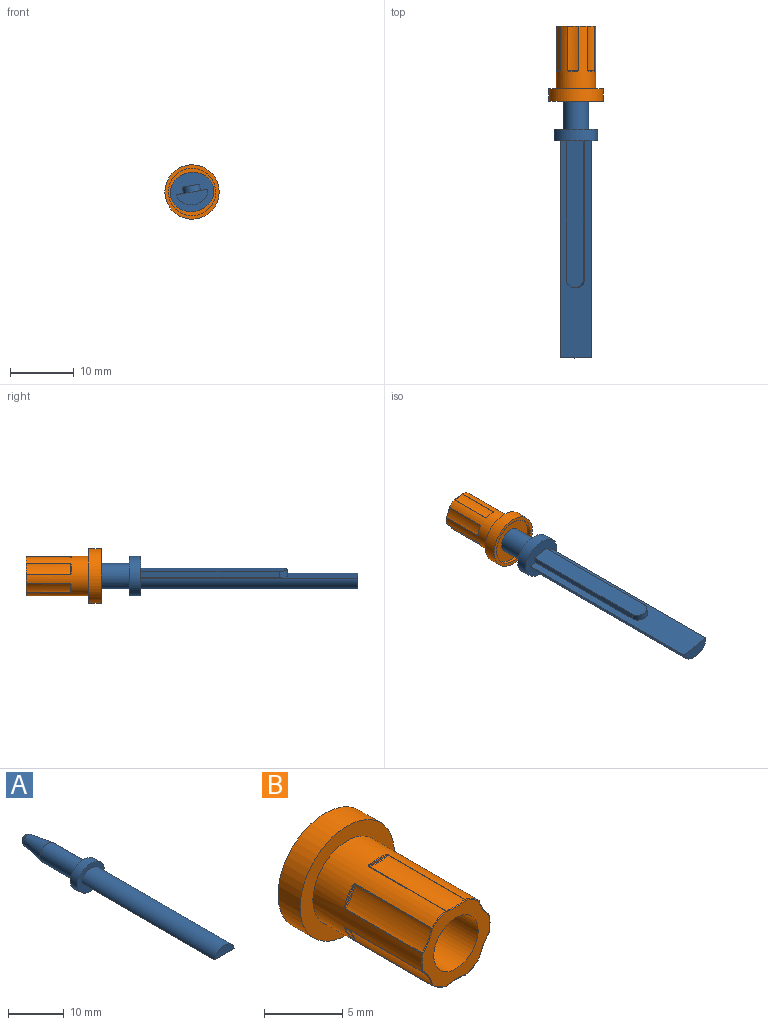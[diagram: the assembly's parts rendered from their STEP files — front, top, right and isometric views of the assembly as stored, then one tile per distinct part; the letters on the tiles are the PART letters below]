
ASSEMBLY  parts=2 mates=1
PART A: 14 faces, bbox 6.9x51x6.1 mm
  f0: plane 6.9x6.1mm, normal (0,-1,0), area 22.7mm2, adj f1,f2,f4,f10,f11,f13
  f1: plane 34x4.9mm, normal (0,0,-1), area 105.3mm2, adj f0,f2,f3,f10,f11,f12
  f2: extruded ~34x4.9mm, area 238.3mm2, adj f0,f1,f3
  f3: plane 4.9x2mm, normal (0,-1,0), area 7.7mm2, adj f1,f2
  f4: extruded ~6.9x6.1mm, area 36.8mm2, adj f0,f5
  f5: plane 6.9x6.1mm, normal (0,1,0), area 20.6mm2, adj f4,f6
  f6: cylinder r=1.99mm len=9.15mm, axis (0,-1,0), area 114.4mm2, adj f5,f8
  f7: plane 0.3x0.3mm, normal (0,1,0), area 0.1mm2, adj f9
  f8: bspline ~5.27x3.98mm, area 52.2mm2, adj f6,f9
  f9: bspline ~2.27x2.27mm, area 6.6mm2, adj f7,f8
  f10: plane 21.65x1mm, normal (-1,0,0), area 21.7mm2, adj f0,f1,f12,f13
  f11: plane 21.65x1mm, normal (1,0,0), area 21.7mm2, adj f0,f1,f12,f13
  f12: cylinder r=1.35mm len=2.7mm, axis (0,0,1), area 4.2mm2, adj f1,f10,f11,f13
  f13: plane 23x2.7mm, normal (0,0,-1), area 61.3mm2, adj f0,f10,f11,f12
PART B: 80 faces, bbox 8.5x11.8x8.5 mm
  f0: cylinder r=2mm len=11.2mm, axis (0,-1,0), area 140.7mm2, adj f5,f79
  f1: cylinder r=4.25mm len=8.5mm, axis (0,1,0), area 53.4mm2, adj f2,f3
  f2: plane 8.5x8.5mm, normal (0,-1,0), area 26.6mm2, adj f1,f4
  f3: plane 8.5x8.5mm, normal (0,1,0), area 13.5mm2, adj f1,f78
  f4: cylinder r=3.1mm len=9.75mm, axis (0,1,0), area 114.6mm2, adj f2,f8,f9,f11,f12,f13,f16,f17
  f5: plane 6.1x5.86mm, normal (0,-1,0), area 14.9mm2, adj f0,f54,f57,f58,f61,f62,f65,f66
  f6: extruded ~6.9x1.7mm, area 11.9mm2, adj f8,f10,f13,f66
  f7: plane 1.38x0.15mm, normal (0,-1,0), area 0.1mm2, adj f10,f11
  f8: cylinder r=0.05mm len=6.9mm, axis (0,-1,0), area 0.2mm2, adj f4,f6,f9,f64
  f9: bspline ~0.21x0.12mm, area 0mm2, adj f4,f8,f10,f11
  f10: bspline ~1.83x0.2mm, area 0.1mm2, adj f6,f7,f9,f12
  f11: torus R=3.05mm, axis (0,-1,0), area 0.1mm2, adj f4,f7,f9,f12
  f12: bspline ~0.31x0.11mm, area 0mm2, adj f4,f10,f11,f13
  f13: cylinder r=0.05mm len=6.9mm, axis (0,-1,0), area 0.2mm2, adj f4,f6,f12,f68
  f14: extruded ~6.9x1.48mm, area 11.9mm2, adj f16,f18,f21,f58
  f15: plane 1.2x0.68mm, normal (0,-1,0), area 0.1mm2, adj f18,f19
  f16: cylinder r=0.05mm len=6.9mm, axis (0,-1,0), area 0.2mm2, adj f4,f14,f17,f56
  f17: bspline ~0.2x0.12mm, area 0mm2, adj f4,f16,f18,f19
  f18: bspline ~1.49x0.87mm, area 0.1mm2, adj f14,f15,f17,f20
  f19: torus R=3.05mm, axis (0,-1,0), area 0.1mm2, adj f4,f15,f17,f20
  f20: bspline ~0.27x0.21mm, area 0mm2, adj f4,f18,f19,f21
  f21: cylinder r=0.05mm len=6.9mm, axis (0,-1,0), area 0.2mm2, adj f4,f14,f20,f60
  f22: extruded ~6.9x1.47mm, area 11.9mm2, adj f24,f26,f29,f57
  f23: plane 1.19x0.7mm, normal (0,-1,0), area 0.1mm2, adj f26,f27
  f24: cylinder r=0.05mm len=6.9mm, axis (0,-1,0), area 0.2mm2, adj f4,f22,f25,f59
  f25: bspline ~0.18x0.15mm, area 0mm2, adj f4,f24,f26,f27
  f26: bspline ~1.57x0.95mm, area 0.1mm2, adj f22,f23,f25,f28
  f27: torus R=3.05mm, axis (0,-1,0), area 0.1mm2, adj f4,f23,f25,f28
  f28: bspline ~0.3x0.16mm, area 0mm2, adj f4,f26,f27,f29
  f29: cylinder r=0.05mm len=6.9mm, axis (0,-1,0), area 0.2mm2, adj f4,f22,f28,f55
  f30: extruded ~6.9x1.7mm, area 11.9mm2, adj f32,f34,f37,f65
  f31: plane 1.38x0.15mm, normal (0,-1,0), area 0.1mm2, adj f34,f35
  f32: cylinder r=0.05mm len=6.9mm, axis (0,-1,0), area 0.2mm2, adj f4,f30,f33,f67
  f33: bspline ~0.21x0.12mm, area 0mm2, adj f4,f32,f34,f35
  f34: bspline ~1.83x0.2mm, area 0.1mm2, adj f30,f31,f33,f36
  f35: torus R=3.05mm, axis (0,-1,0), area 0.1mm2, adj f4,f31,f33,f36
  f36: bspline ~0.31x0.11mm, area 0mm2, adj f4,f34,f35,f37
  f37: cylinder r=0.05mm len=6.9mm, axis (0,-1,0), area 0.2mm2, adj f4,f30,f36,f63
  f38: extruded ~6.9x1.48mm, area 11.9mm2, adj f40,f42,f45,f73
  f39: plane 1.2x0.68mm, normal (0,-1,0), area 0.1mm2, adj f42,f43
  f40: cylinder r=0.05mm len=6.9mm, axis (0,-1,0), area 0.2mm2, adj f4,f38,f41,f75
  f41: bspline ~0.2x0.12mm, area 0mm2, adj f4,f40,f42,f43
  f42: bspline ~1.49x0.87mm, area 0.1mm2, adj f38,f39,f41,f44
  f43: torus R=3.05mm, axis (0,-1,0), area 0.1mm2, adj f4,f39,f41,f44
  f44: bspline ~0.27x0.21mm, area 0mm2, adj f4,f42,f43,f45
  f45: cylinder r=0.05mm len=6.9mm, axis (0,-1,0), area 0.2mm2, adj f4,f38,f44,f71
  f46: extruded ~6.9x1.47mm, area 11.9mm2, adj f48,f50,f53,f74
  f47: plane 1.19x0.7mm, normal (0,-1,0), area 0.1mm2, adj f50,f51
  f48: cylinder r=0.05mm len=6.9mm, axis (0,-1,0), area 0.2mm2, adj f4,f46,f49,f72
  f49: bspline ~0.18x0.15mm, area 0mm2, adj f4,f48,f50,f51
  f50: bspline ~1.57x0.95mm, area 0.1mm2, adj f46,f47,f49,f52
  f51: torus R=3.05mm, axis (0,-1,0), area 0.1mm2, adj f4,f47,f49,f52
  f52: bspline ~0.3x0.16mm, area 0mm2, adj f4,f50,f51,f53
  f53: cylinder r=0.05mm len=6.9mm, axis (0,-1,0), area 0.2mm2, adj f4,f46,f52,f76
  f54: torus R=3.05mm, axis (0,-1,0), area 0.1mm2, adj f4,f5,f55,f56
  f55: sphere r=0.05mm, area 0mm2, adj f29,f54,f57
  f56: sphere r=0.05mm, area 0mm2, adj f16,f54,f58
  f57: bspline ~1.62x0.97mm, area 0.1mm2, adj f5,f22,f55,f59
  f58: bspline ~1.63x0.96mm, area 0.1mm2, adj f5,f14,f56,f60
  f59: sphere r=0.05mm, area 0mm2, adj f24,f57,f61
  f60: sphere r=0.05mm, area 0mm2, adj f21,f58,f62
  f61: torus R=3.05mm, axis (0,-1,0), area 0.1mm2, adj f4,f5,f59,f63
  f62: torus R=3.05mm, axis (0,-1,0), area 0.1mm2, adj f4,f5,f60,f64
  f63: sphere r=0.05mm, area 0mm2, adj f37,f61,f65
  f64: sphere r=0.05mm, area 0mm2, adj f8,f62,f66
  f65: bspline ~1.87x0.2mm, area 0.1mm2, adj f5,f30,f63,f67
  f66: bspline ~1.87x0.2mm, area 0.1mm2, adj f5,f6,f64,f68
  f67: sphere r=0.05mm, area 0mm2, adj f32,f65,f69
  f68: sphere r=0.05mm, area 0mm2, adj f13,f66,f70
  f69: torus R=3.05mm, axis (0,-1,0), area 0.1mm2, adj f4,f5,f67,f71
  f70: torus R=3.05mm, axis (0,-1,0), area 0.1mm2, adj f4,f5,f68,f72
  f71: sphere r=0.05mm, area 0mm2, adj f45,f69,f73
  f72: sphere r=0.05mm, area 0mm2, adj f48,f70,f74
  f73: bspline ~1.63x0.96mm, area 0.1mm2, adj f5,f38,f71,f75
  f74: bspline ~1.62x0.97mm, area 0.1mm2, adj f5,f46,f72,f76
  f75: sphere r=0.05mm, area 0mm2, adj f40,f73,f77
  f76: sphere r=0.05mm, area 0mm2, adj f53,f74,f77
  f77: torus R=3.05mm, axis (0,-1,0), area 0.1mm2, adj f4,f5,f75,f76
  f78: cylinder r=3.71mm len=7.42mm, axis (0,1,0), area 14mm2, adj f3,f79
  f79: plane 7.42x7.42mm, normal (0,1,0), area 30.7mm2, adj f0,f78
PLACE A rot(axis=(0,1,0),169.9deg) t=(5.84,-9.57,-14.67)mm fixed
PLACE B rot(axis=(-0.08,0,1),180deg) t=(5.84,30.62,-14.67)mm
MATE cylindrical B.f0 <-> A.f6  axis (0,1,0) through (5.84,31.22,-14.67)mm
